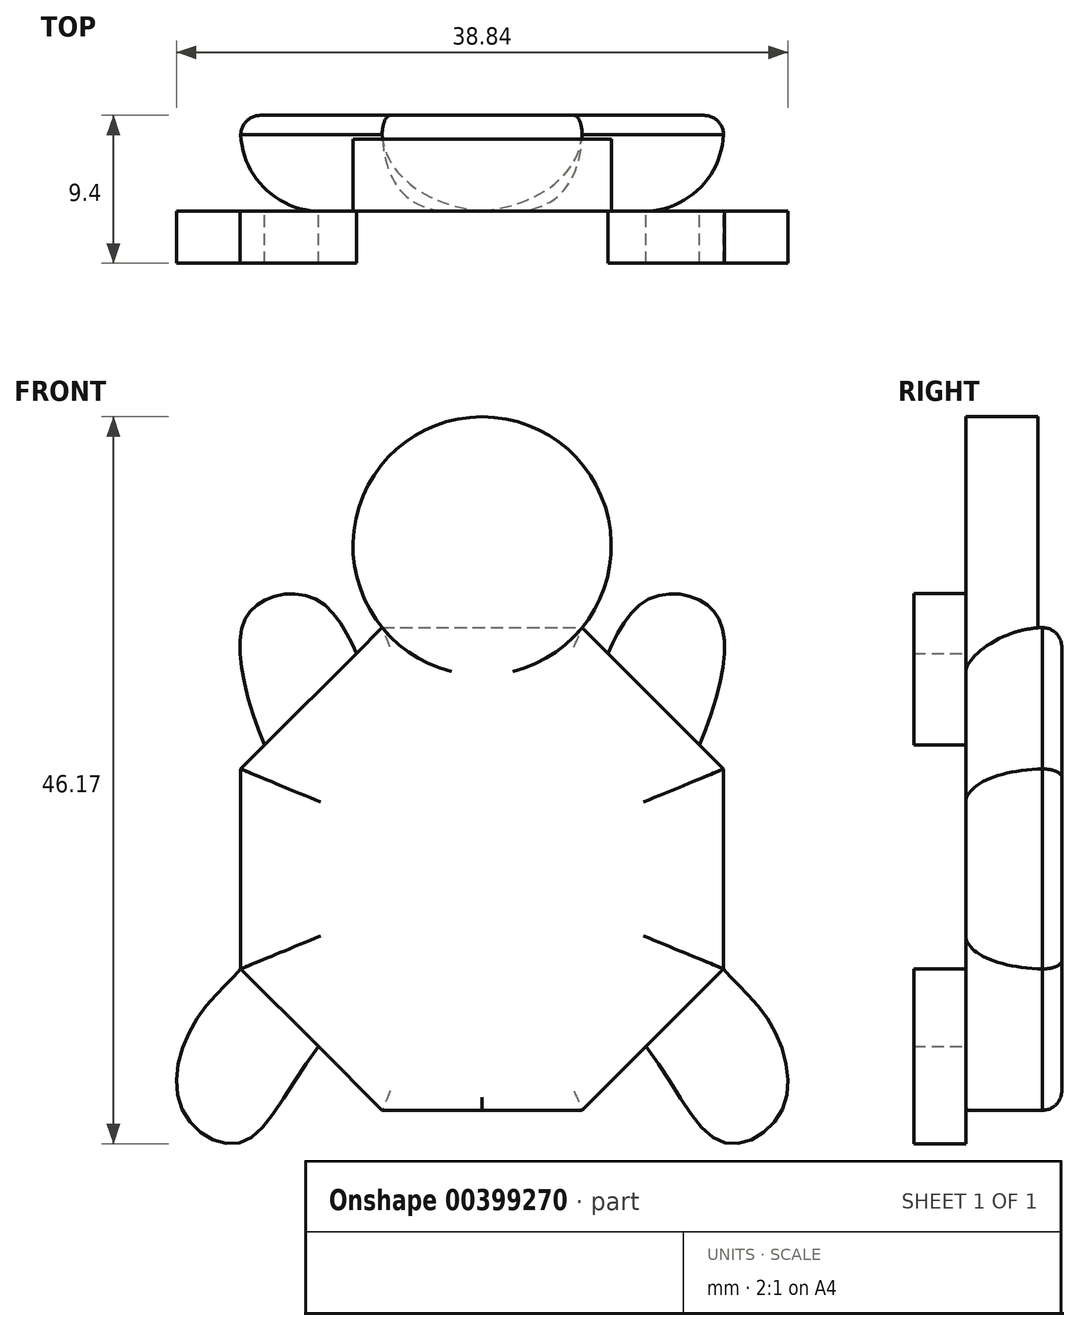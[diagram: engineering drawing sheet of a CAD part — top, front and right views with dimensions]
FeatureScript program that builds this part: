
annotation { "Feature Type Name" : "Feature", "Feature Type Description" : "" }
export const myFeature = defineFeature(function(context is Context, id is Id, definition is map)
    precondition{}
    {
        {
            var Q0;
            Q0=qCreatedBy(makeId("Front.planeOp"),FACE);
            var sketch = newSketch(context, id + "F0", { "sketchPlane" : qUnion([Q0])});
            skCircle(sketch, "E0.cCircle", {"center": v(0, 0) * mm, "radius": 15.33 * mm, "construction": true});
            skLineSegment(sketch, "E0.0", {"start": v(6.35, -15.33) * mm, "end": v(-6.35, -15.33) * mm});
            skLineSegment(sketch, "E0.1", {"start": v(-6.35, -15.33) * mm, "end": v(-15.33, -6.35) * mm});
            skLineSegment(sketch, "E0.2", {"start": v(-15.33, -6.35) * mm, "end": v(-15.33, 6.35) * mm});
            skLineSegment(sketch, "E0.3", {"start": v(-15.33, 6.35) * mm, "end": v(-6.35, 15.33) * mm});
            skLineSegment(sketch, "E0.4", {"start": v(-6.35, 15.33) * mm, "end": v(6.35, 15.33) * mm});
            skLineSegment(sketch, "E0.5", {"start": v(6.35, 15.33) * mm, "end": v(15.33, 6.35) * mm});
            skLineSegment(sketch, "E0.6", {"start": v(15.33, 6.35) * mm, "end": v(15.33, -6.35) * mm});
            skLineSegment(sketch, "E0.7", {"start": v(15.33, -6.35) * mm, "end": v(6.35, -15.33) * mm});
            skPoint(sketch, "E0.0.midPoint", {"position": v(0, -15.33) * mm});
            skArc(sketch, "E1", {"start": v(6.35, 15.33) * mm, "mid": v(0, 28.72) * mm, "end": v(-6.35, 15.33) * mm});
            skFitSpline(sketch, "E2", {"points": [v(15.33, -6.35) * mm, v(18.18, -9.6) * mm, v(19.06, -15.29) * mm, v(15.33, -17.36) * mm, v(10.4, -11.28) * mm], "startDerivative": vector(7.96, -10.06) * mm, "endDerivative": vector(-19.31, 24.24) * mm});
            skPoint(sketch, "E3.2.internal.snap0", {"position": v(10.84, -10.84) * mm});
            skFitSpline(sketch, "E4", {"points": [v(7.99, 13.7) * mm, v(10.4, 17.04) * mm, v(13.68, 17.14) * mm, v(15.33, 14.94) * mm, v(13.8, 7.88) * mm], "startDerivative": vector(5.68, 13.33) * mm, "endDerivative": vector(-9.21, -21) * mm});
            skFitSpline(sketch, "E5.MirrorCS", {"points": [v(-15.33, -6.35) * mm, v(-18.18, -9.6) * mm, v(-19.06, -15.29) * mm, v(-15.33, -17.36) * mm, v(-10.4, -11.28) * mm], "startDerivative": vector(-7.96, -10.06) * mm, "endDerivative": vector(19.31, 24.24) * mm});
            skFitSpline(sketch, "E6.MirrorCS", {"points": [v(-7.99, 13.7) * mm, v(-10.4, 17.04) * mm, v(-13.68, 17.14) * mm, v(-15.33, 14.94) * mm, v(-13.8, 7.88) * mm], "startDerivative": vector(-5.68, 13.33) * mm, "endDerivative": vector(9.21, -21) * mm});
            skSolve(sketch);
        }
        {
            var Q0;
            {var subQ11=sQuery(id+"F0.wireOp",EDGE,"E0.0");Q0=makeQuery(id+"F0.imprint","IMPRINT",FACE,{"disambiguationData":[TD([[makeQuery(id+"F0.imprint","IMPRINT",EDGE,{"derivedFrom":subQ11}),-1.0]])]});}
            extrude(context, id + "F1", {"entities" : qUnion([Q0]), "oppositeDirection" : true, "depth" : 6.1 * mm});
        }
        {
            var Q0;
            {var subQ0=sQuery(id+"F0.wireOp",EDGE,"E4");Q0=makeQuery(id+"F0.imprint","IMPRINT",FACE,{"disambiguationData":[TD([[makeQuery(id+"F0.imprint","IMPRINT",EDGE,{"derivedFrom":subQ0}),-1.0]])]});}
            var Q1;
            {var subQ0=sQuery(id+"F0.wireOp",EDGE,"E6.MirrorCS");Q1=makeQuery(id+"F0.imprint","IMPRINT",FACE,{"disambiguationData":[TD([[makeQuery(id+"F0.imprint","IMPRINT",EDGE,{"derivedFrom":subQ0}),1.0]])]});}
            var Q2;
            {var subQ0=sQuery(id+"F0.wireOp",EDGE,"E5.MirrorCS");Q2=makeQuery(id+"F0.imprint","IMPRINT",FACE,{"disambiguationData":[TD([[makeQuery(id+"F0.imprint","IMPRINT",EDGE,{"derivedFrom":subQ0}),1.0]])]});}
            var Q3;
            {var subQ0=sQuery(id+"F0.wireOp",EDGE,"E2");Q3=makeQuery(id+"F0.imprint","IMPRINT",FACE,{"disambiguationData":[TD([[makeQuery(id+"F0.imprint","IMPRINT",EDGE,{"derivedFrom":subQ0}),-1.0]])]});}
            extrude(context, id + "F2", {"entities" : qUnion([Q0, Q1, Q2, Q3]), "operationType" : NewBodyOperationType.ADD, "depth" : 3.3 * mm});
        }
        {
            var Q0;
            Q0=makeQuery(id+"F0.imprint","IMPRINT",FACE,{"disambiguationData":[TD([[makeQuery(id+"F0.imprint","IMPRINT",EDGE,{"derivedFrom":sQuery(id+"F0.wireOp",EDGE,"E0.4")}),1.0]])]});
            extrude(context, id + "F3", {"entities" : qUnion([Q0]), "operationType" : NewBodyOperationType.ADD, "oppositeDirection" : true, "depth" : 4.57 * mm});
        }
        {
            var Q0;
            Q0=makeQuery(id+"F1.opExtrude","CAP_EDGE",EDGE,{"disambiguationData":[OSD([sQuery(id+"F0.wireOp",EDGE,"E0.3")])],"isStart":false});
            var Q1;
            Q1=makeQuery(id+"F1.opExtrude","CAP_EDGE",EDGE,{"disambiguationData":[OSD([sQuery(id+"F0.wireOp",EDGE,"E0.2")])],"isStart":false});
            var Q2;
            Q2=makeQuery(id+"F1.opExtrude","CAP_EDGE",EDGE,{"disambiguationData":[OSD([sQuery(id+"F0.wireOp",EDGE,"E0.1")])],"isStart":false});
            var Q3;
            Q3=makeQuery(id+"F1.opExtrude","CAP_EDGE",EDGE,{"disambiguationData":[OSD([sQuery(id+"F0.wireOp",EDGE,"E0.0")])],"isStart":false});
            var Q4;
            Q4=makeQuery(id+"F1.opExtrude","CAP_EDGE",EDGE,{"disambiguationData":[OSD([sQuery(id+"F0.wireOp",EDGE,"E0.7")])],"isStart":false});
            var Q5;
            Q5=makeQuery(id+"F1.opExtrude","CAP_EDGE",EDGE,{"disambiguationData":[OSD([sQuery(id+"F0.wireOp",EDGE,"E0.6")])],"isStart":false});
            var Q6;
            Q6=makeQuery(id+"F1.opExtrude","CAP_EDGE",EDGE,{"disambiguationData":[OSD([sQuery(id+"F0.wireOp",EDGE,"E0.5")])],"isStart":false});
            var Q7;
            Q7=makeQuery(id+"F1.opExtrude","CAP_FACE",FACE,{"disambiguationData":[OSD([sQuery(id+"F0.wireOp",EDGE,"E0.0"),sQuery(id+"F0.wireOp",EDGE,"E0.1"),sQuery(id+"F0.wireOp",EDGE,"E0.2"),sQuery(id+"F0.wireOp",EDGE,"E0.3"),sQuery(id+"F0.wireOp",EDGE,"E0.4"),sQuery(id+"F0.wireOp",EDGE,"E0.5"),sQuery(id+"F0.wireOp",EDGE,"E0.6"),sQuery(id+"F0.wireOp",EDGE,"E0.7")])],"isStart":false});
            fillet(context, id + "F4", {"entities" : qUnion([Q0, Q1, Q2, Q3, Q4, Q5, Q6, Q7]), "radius" : 1.23 * mm, "tangentPropagation" : true, "allowEdgeOverflow" : false});
        }
        {
            var Q0;
            Q0=makeQuery(id+"F1.opExtrude","CAP_EDGE",EDGE,{"disambiguationData":[OSD([sQuery(id+"F0.wireOp",EDGE,"E0.2")])],"isStart":true});
            var Q1;
            Q1=makeQuery(id+"F1.opExtrude","CAP_EDGE",EDGE,{"disambiguationData":[OSD([sQuery(id+"F0.wireOp",EDGE,"E0.1")])],"isStart":true});
            var Q2;
            Q2=makeQuery(id+"F1.opExtrude","CAP_EDGE",EDGE,{"disambiguationData":[OSD([sQuery(id+"F0.wireOp",EDGE,"E0.7")])],"isStart":true});
            var Q3;
            Q3=makeQuery(id+"F1.opExtrude","CAP_EDGE",EDGE,{"disambiguationData":[OSD([sQuery(id+"F0.wireOp",EDGE,"E0.6")])],"isStart":true});
            var Q4;
            Q4=makeQuery(id+"F1.opExtrude","CAP_EDGE",EDGE,{"disambiguationData":[OSD([sQuery(id+"F0.wireOp",EDGE,"E0.5")])],"isStart":true});
            var Q5;
            Q5=makeQuery(id+"F1.opExtrude","CAP_EDGE",EDGE,{"disambiguationData":[OSD([sQuery(id+"F0.wireOp",EDGE,"E0.3")])],"isStart":true});
            fillet(context, id + "F5", {"entities" : qUnion([Q0, Q1, Q2, Q3, Q4, Q5]), "radius" : 5.08 * mm, "tangentPropagation" : true, "allowEdgeOverflow" : false});
        }
    });
